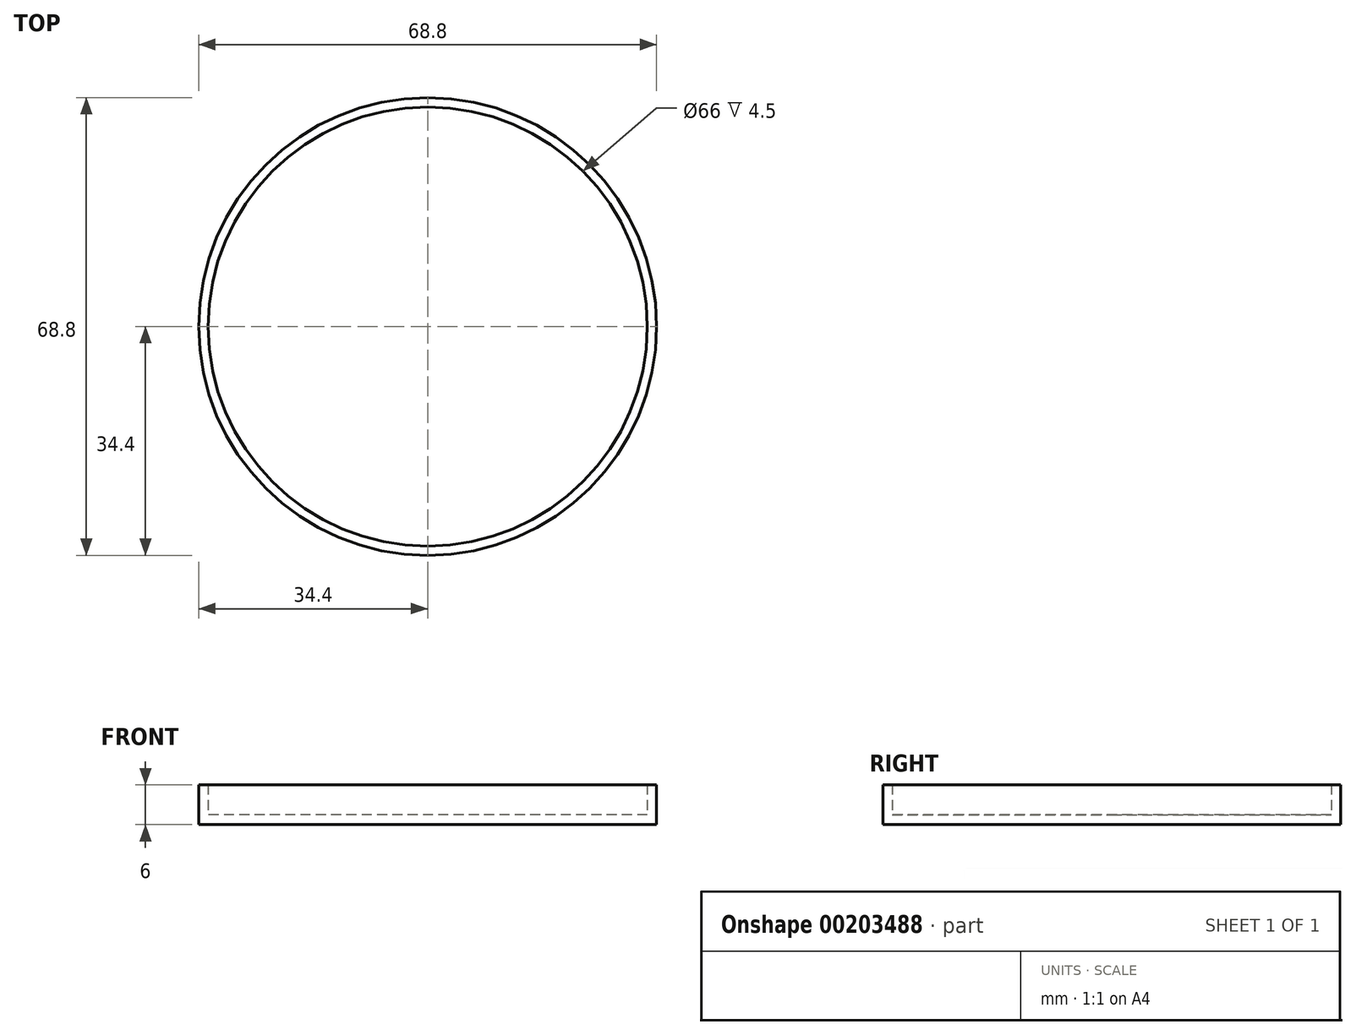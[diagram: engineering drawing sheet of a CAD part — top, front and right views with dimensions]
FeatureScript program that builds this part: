
annotation { "Feature Type Name" : "Feature", "Feature Type Description" : "" }
export const myFeature = defineFeature(function(context is Context, id is Id, definition is map)
    precondition{}
    {
        {
            var Q0;
            Q0=qCreatedBy(makeId("Top.planeOp"),FACE);
            var sketch = newSketch(context, id + "F0", { "sketchPlane" : qUnion([Q0])});
            skCircle(sketch, "E0", {"center": v(0, 0) * mm, "radius": 33.5 * mm});
            skSolve(sketch);
        }
        {
            var Q0;
            Q0=makeQuery(id+"F0.imprint","IMPRINT",FACE,{"disambiguationData":[TD([[makeQuery(id+"F0.imprint","IMPRINT",EDGE,{"derivedFrom":sQuery(id+"F0.wireOp",EDGE,"E0")}),1.0]])]});
            extrude(context, id + "F1", {"entities" : qUnion([Q0]), "depth" : 1.5 * mm});
        }
        {
            var Q0;
            Q0=qCreatedBy(makeId("Top.planeOp"),FACE);
            var sketch = newSketch(context, id + "F2", { "sketchPlane" : qUnion([Q0])});
            skCircle(sketch, "E1", {"center": v(0, 0) * mm, "radius": 33 * mm});
            skCircle(sketch, "E2", {"center": v(0, 0) * mm, "radius": 34.4 * mm});
            skSolve(sketch);
        }
        {
            var Q0;
            Q0=makeQuery(id+"F2.imprint","IMPRINT",FACE,{"disambiguationData":[TD([[makeQuery(id+"F2.imprint","IMPRINT",EDGE,{"derivedFrom":sQuery(id+"F2.wireOp",EDGE,"E1")}),-1.0]])]});
            extrude(context, id + "F3", {"entities" : qUnion([Q0]), "operationType" : NewBodyOperationType.ADD, "depth" : 6 * mm});
        }
        {
            var Q0;
            Q0=sQuery(id+"F2.wireOp",EDGE,"E1");
            var Q1;
            Q1=sQuery(id+"F2.wireOp",EDGE,"E2");
            extrude(context, id + "F4", {"bodyType" : ToolBodyType.SURFACE, "surfaceEntities" : qUnion([Q0, Q1]), "depth" : 5 * mm});
        }
    });
